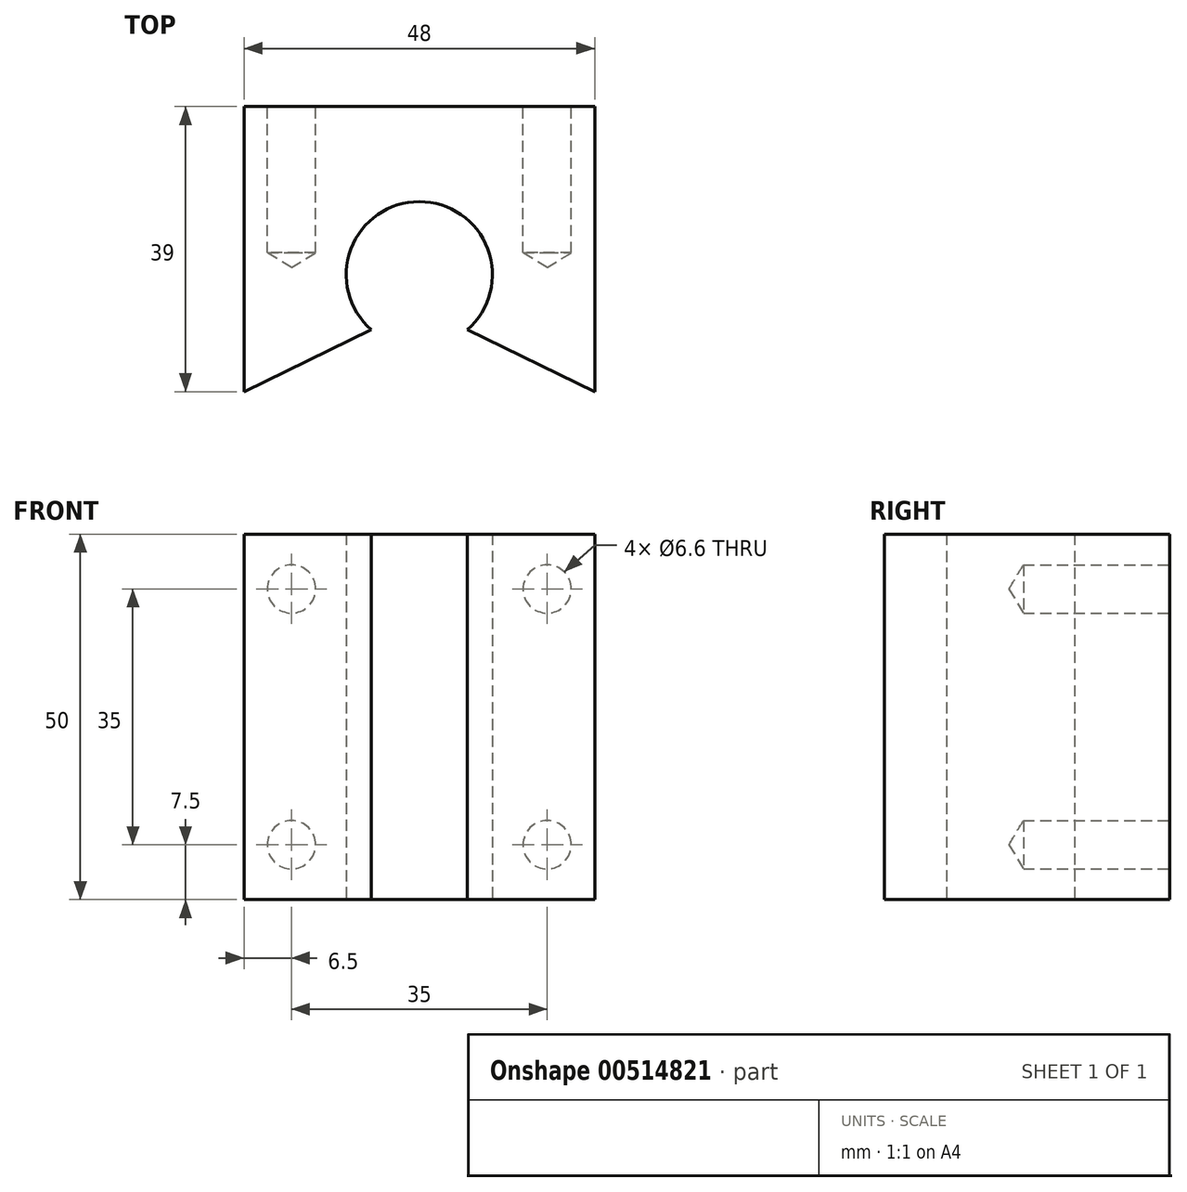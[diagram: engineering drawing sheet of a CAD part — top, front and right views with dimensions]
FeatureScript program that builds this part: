
annotation { "Feature Type Name" : "Feature", "Feature Type Description" : "" }
export const myFeature = defineFeature(function(context is Context, id is Id, definition is map)
    precondition{}
    {
        {
            var Q0;
            Q0=qCreatedBy(makeId("Top.planeOp"),FACE);
            var sketch = newSketch(context, id + "F0", { "sketchPlane" : qUnion([Q0])});
            skLineSegment(sketch, "E0.bottom", {"start": v(609.6, 602.09) * mm, "end": v(-609.6, 602.09) * mm});
            skLineSegment(sketch, "E0.top", {"start": v(609.6, -602.09) * mm, "end": v(-609.6, -602.09) * mm});
            skLineSegment(sketch, "E0.left", {"start": v(609.6, 602.09) * mm, "end": v(609.6, -602.09) * mm});
            skLineSegment(sketch, "E0.right", {"start": v(-609.6, 602.09) * mm, "end": v(-609.6, -602.09) * mm});
            skLineSegment(sketch, "E1.bottom", {"start": v(0, 0) * mm, "end": v(48, 0) * mm});
            skLineSegment(sketch, "E1.top", {"start": v(0, 39) * mm, "end": v(48, 39) * mm});
            skLineSegment(sketch, "E1.left", {"start": v(0, 0) * mm, "end": v(0, 39) * mm});
            skLineSegment(sketch, "E1.right", {"start": v(48, 0) * mm, "end": v(48, 39) * mm});
            skLineSegment(sketch, "E2", {"start": v(0, 0) * mm, "end": v(17.42, 8.47) * mm});
            skArc(sketch, "E3", {"start": v(17.42, 8.47) * mm, "mid": v(24, 26) * mm, "end": v(30.58, 8.47) * mm});
            skLineSegment(sketch, "E4", {"start": v(30.58, 8.47) * mm, "end": v(48, 0) * mm});
            skSolve(sketch);
        }
        {
            var Q0;
            Q0=makeQuery(id+"F0.imprint","IMPRINT",FACE,{"disambiguationData":[TD([[makeQuery(id+"F0.imprint","IMPRINT",EDGE,{"derivedFrom":sQuery(id+"F0.wireOp",EDGE,"LKlDstmL-CMEF-P5RP-QhqV-0Ih8qj4wdOus.bottom")}),1.0]])]});
            var Q1;
            Q1=makeQuery(id+"F0.imprint","IMPRINT",FACE,{"disambiguationData":[TD([[makeQuery(id+"F0.imprint","IMPRINT",EDGE,{"derivedFrom":sQuery(id+"F0.wireOp",EDGE,"E1.top")}),-1.0]])]});
            extrude(context, id + "F1", {"entities" : qUnion([Q0, Q1]), "depth" : 50 * mm, "offsetDistance" : 25 * mm});
        }
        {
            var Q0;
            Q0=makeQuery(id+"F1.opExtrude","SWEPT_FACE",FACE,{"disambiguationData":[OSD([sQuery(id+"F0.wireOp",EDGE,"E1.top")])]});
            var sketch = newSketch(context, id + "F2", { "sketchPlane" : qUnion([Q0])});
            skPoint(sketch, "E5", {"position": v(-41.5, 42.5) * mm});
            skPoint(sketch, "E6", {"position": v(-6.5, 42.5) * mm});
            skPoint(sketch, "E7", {"position": v(-6.5, 7.5) * mm});
            skPoint(sketch, "E8", {"position": v(-41.5, 7.5) * mm});
            skSolve(sketch);
        }
        {
            var Q0;
            Q0=sQuery(id+"F2.wireOp",VERTEX,"E5");
            var Q1;
            Q1=sQuery(id+"F2.wireOp",VERTEX,"E8");
            var Q2;
            Q2=sQuery(id+"F2.wireOp",VERTEX,"E7");
            var Q3;
            Q3=sQuery(id+"F2.wireOp",VERTEX,"E6");
            var Q4;
            Q4=makeQuery(id+"F1.opExtrude","SWEPT_BODY",BODY,{"disambiguationData":[OSD([sQuery(id+"F0.wireOp",EDGE,"E1.top"),sQuery(id+"F0.wireOp",EDGE,"E1.left"),sQuery(id+"F0.wireOp",EDGE,"E1.right"),sQuery(id+"F0.wireOp",EDGE,"E2"),sQuery(id+"F0.wireOp",EDGE,"E3"),sQuery(id+"F0.wireOp",EDGE,"E4")])]});
            hole(context, id + "F3", {"style" : HoleStyle.SIMPLE, "endStyle" : HoleEndStyle.BLIND, "standardTappedOrClearance" : lookupTablePath({ "standard" : "ISO", "fit" : "Normal", "size" : "M6", "type" : "Clearance" }), "standardBlindInLast" : lookupTablePath({ "fit" : "Standard", "standard" : "ISO", "size" : "M6", "type" : "Clearance" }), "holeDiameter" : 6.6 * mm, "holeDepth" : 20 * mm, "isTappedThrough" : true, "tappedDepth" : 12 * mm, "tapClearance" : 3, "locations" : qUnion([Q0, Q1, Q2, Q3]), "scope" : qUnion([Q4])});
        }
    });
